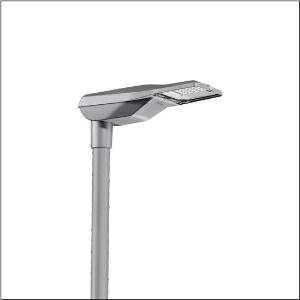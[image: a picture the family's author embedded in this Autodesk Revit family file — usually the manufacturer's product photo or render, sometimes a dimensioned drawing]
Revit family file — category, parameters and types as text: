
# Revit family: streetlight_sl_21_iq_micro___st1_0ab_5xe1m31g08db_d575
name_source: partatom
category: Lighting Fixtures
units: mm (PartAtom-declared; Revit-internal decimal feet)

## family parameters
Cut with Voids When Loaded = No
Host = Face
Light Source = No
Part Type = Normal
Room Calculation Point = No
Round Connector Dimension = Use Diameter
Shared = No

## types (1)
- --- (1 x LED, 4240 lm, 36.4 W, 3000K)
    Apparent Load = 36 VA
    CIE Flux Codes = 38 73 97 100 100
    Color Rendering = 70
    Color Temperature = 3000K
    Default Elevation = 1800 mm
    Description = Streetlight SL 21 iQ micro, mast luminaire, primary light control with lens, of PMMA, primary optical cover: cover, of toughened safety glass, transparent, light distribution: ST1.0aB, light emission: direct distribution, primary light characteristic: asymmetric, installation type: post-top, side-entry, LED, High Power LED, rated luminous flux: 4.240lm, luminous efficacy: 117lm/W, light colour: 730, colour temperature: 3000K, control gear: iQ Street-Remote, control: Street-Remote, Auto-Match, Temp-Guard, Lumen-Switch, Night-Set, Smart-Wire, Light-Fading, Desk-Remote (wireless, voltage-free reading and setting of iQ features in the workshop via application-optimized NFC function/RFID function), optimised constant luminous flux control (CLO 2.0), pre-setting: linear dimming characteristic, mains connection: 220..240V, AC, 50/60Hz, start of lifetime: 36W, end of service life: 38W, reduction: 16W, luminaire housing, of diecast aluminium, powder-coated, Siteco® metallic grey (DB 702S), corrosivity category C5 high according to DIN EN ISO 12944, please order mast flange separately, inclination adjustable: 0°, 5°, 10°, 15°, sealing non-destructively replaceable, multi-level sealing system, length: 528mm, width: 235mm, height: 110mm, mast flange for spigot size: 42mm (side-entry): 5XC10008XM4, 60/48mm (side-entry/post-top): 5XC10108XM2, 76/60mm (side-entry/post-top): 5XC10108XM1, protection rating (complete): IP66, insulation class (complete): insulation class II (safety insulation), certification: CE, ENEC, ENEC+, VDE, impact resistance: IK10, permissible operating ambient temperature for outdoor applications: -40..+50°C, standard-compliant lighting for roads and squares, packaging unit: 1 piece

Light Distribution: ST1.0aB
    Height = 110 mm
    Lamp = 1 x LED
    Lamp Light Flux = 4240 lm
    Lamp Power = 36.4 W
    Lamp count = 1
    Length = 528 mm
    Luminous efficacy = 116 lm/W
    Manufacturer = Siteco
    ModVariant = No
    Model = 5XE1M31G08DB
    Number of Poles = 1
    OnlyDefault = Yes
    Power Factor = 1
    Product Name = Streetlight SL 21 iQ micro | ST1.0aB
    Product group = mast luminaire | pylon top
    ProductGroupID = 6100
    Protection Class = Protection class II
    Protection Degree = IP 66
    RLX_Detail_Level = 1
    RLX_Emergency_Light_Flux = 0 lm
    RLX_Emergency_Type = 0
    RLX_Emergency_Type_DB = No
    RlxData = <blob elided: 99085 chars, md5=e2e8c240>
    Socket = socket
    Standby Power = 0 W
    System Light Flux = 4240 lm
    System Power = 36 W
    Type Comments = factory setting: luminous flux: 100 % | dim-lin: 254 | 715 mA
    Type Image = l_1006881.jpg
    URL = http://relux.com
    VarID = @adj_157327
    Voltage = 0 V
    Weight = 0.00 kg
    Width = 235 mm

## geometry (parser evidence)
native form markers: Blend x4, Sweep x10
no freeform markers — native parametric forms only
